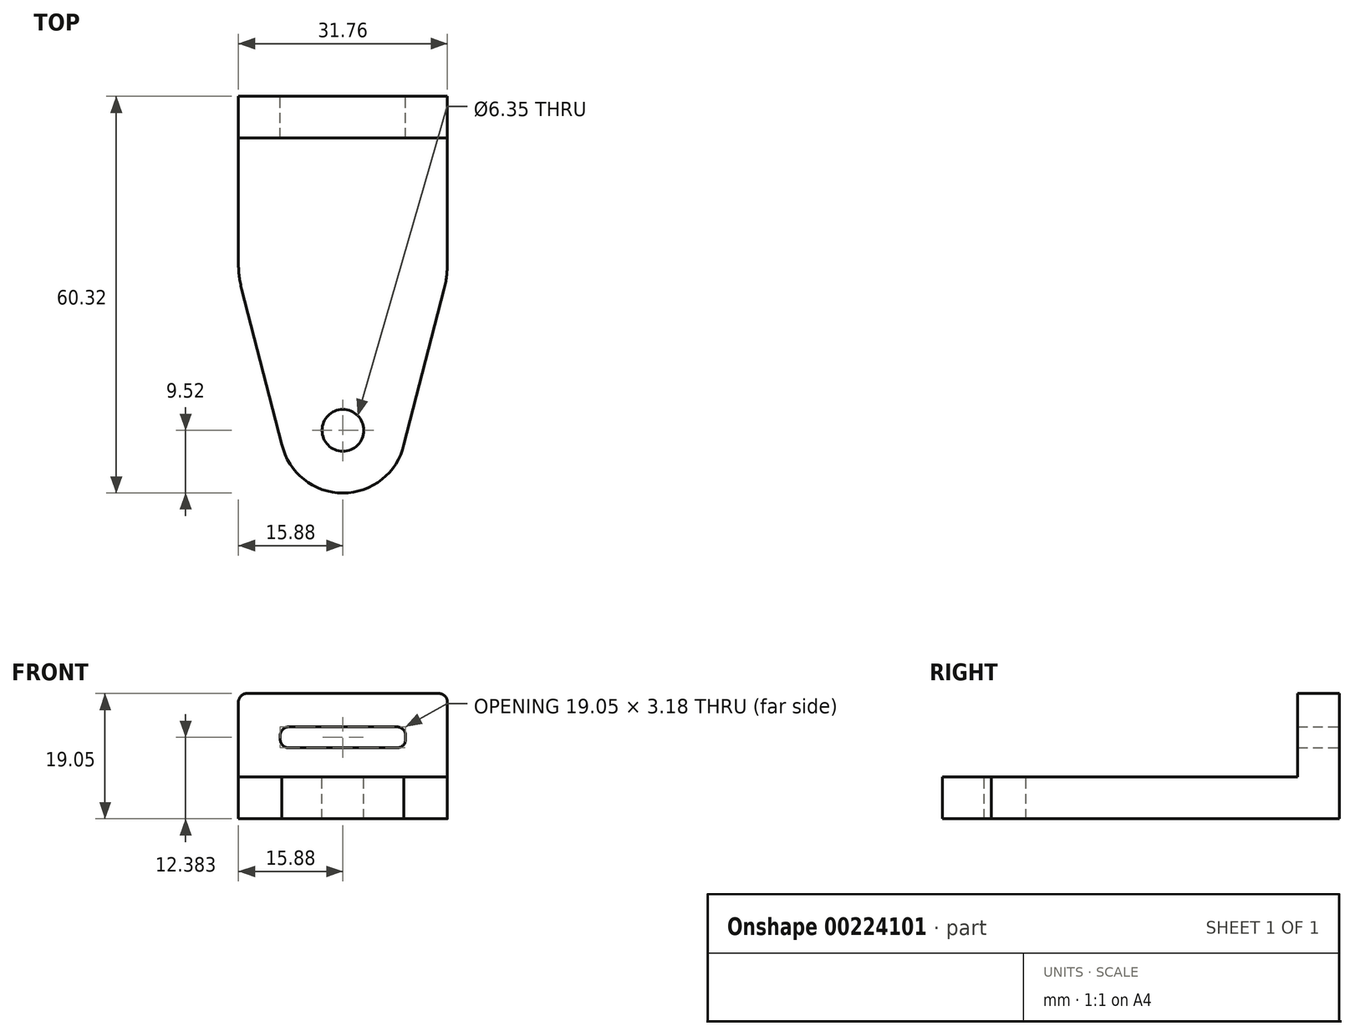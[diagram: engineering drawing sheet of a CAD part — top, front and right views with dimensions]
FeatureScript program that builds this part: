
annotation { "Feature Type Name" : "Feature", "Feature Type Description" : "" }
export const myFeature = defineFeature(function(context is Context, id is Id, definition is map)
    precondition{}
    {
        {
            var Q0;
            Q0=qCreatedBy(makeId("Top.planeOp"),FACE);
            var sketch = newSketch(context, id + "F0", { "sketchPlane" : qUnion([Q0])});
            skCircle(sketch, "E0", {"center": v(0, 0) * mm, "radius": 12.7 * mm});
            skCircle(sketch, "E1.0", {"center": v(0, 0) * mm, "radius": 15.88 * mm});
            skSolve(sketch);
        }
        {
            var Q0;
            Q0=makeQuery(id+"F0.imprint","IMPRINT",FACE,{"disambiguationData":[TD([[makeQuery(id+"F0.imprint","IMPRINT",EDGE,{"derivedFrom":sQuery(id+"F0.wireOp",EDGE,"E0")}),-1.0]])]});
            extrude(context, id + "F1", {"entities" : qUnion([Q0]), "depth" : 6.35 * mm});
        }
        {
            var Q0;
            Q0=qCreatedBy(makeId("Top.planeOp"),FACE);
            var sketch = newSketch(context, id + "F2", { "sketchPlane" : qUnion([Q0])});
            skLineSegment(sketch, "E2.bottom", {"start": v(-15.88, 0) * mm, "end": v(15.88, 0) * mm});
            skLineSegment(sketch, "E2.top", {"start": v(-15.88, 25.4) * mm, "end": v(15.87, 25.4) * mm});
            skLineSegment(sketch, "E2.left", {"start": v(-15.88, 0) * mm, "end": v(-15.88, 25.4) * mm});
            skLineSegment(sketch, "E2.right", {"start": v(15.88, 0) * mm, "end": v(15.87, 25.4) * mm});
            skSolve(sketch);
        }
        {
            var Q0;
            Q0=makeQuery(id+"F2.imprint","IMPRINT",FACE,{"disambiguationData":[TD([[makeQuery(id+"F2.imprint","IMPRINT",EDGE,{"derivedFrom":sQuery(id+"F2.wireOp",EDGE,"E2.bottom")}),1.0]])]});
            extrude(context, id + "F3", {"entities" : qUnion([Q0]), "operationType" : NewBodyOperationType.ADD, "depth" : 6.35 * mm});
        }
        {
            var Q0;
            {var subQ0=sQuery(id+"F2.wireOp",EDGE,"E2.top");var subQ1=sQuery(id+"F2.wireOp",EDGE,"E2.left");var subQ2=sQuery(id+"F2.wireOp",EDGE,"E2.right");Q0=makeQuery(id+"F3.boolean.opBoolean","SPLIT",FACE,{"disambiguationData":[TD([makeQuery(id+"F1.opExtrude","SWEPT_FACE",FACE,{"disambiguationData":[OSD([sQuery(id+"F0.wireOp",EDGE,"E1.0")])]})])],"derivedFrom":makeQuery(id+"F3.opExtrude","CAP_FACE",FACE,{"disambiguationData":[OSD([sQuery(id+"F2.wireOp",EDGE,"E2.bottom"),subQ0,subQ1,subQ2])],"isStart":false})});}
            var sketch = newSketch(context, id + "F4", { "sketchPlane" : qUnion([Q0])});
            skLineSegment(sketch, "E3.bottom", {"start": v(-15.88, 25.4) * mm, "end": v(15.87, 25.4) * mm});
            skLineSegment(sketch, "E3.top", {"start": v(-15.88, 19.05) * mm, "end": v(15.87, 19.05) * mm});
            skLineSegment(sketch, "E3.left", {"start": v(-15.88, 25.4) * mm, "end": v(-15.88, 19.05) * mm});
            skLineSegment(sketch, "E3.right", {"start": v(15.87, 25.4) * mm, "end": v(15.87, 19.05) * mm});
            skSolve(sketch);
        }
        {
            var Q0;
            Q0 = qSketchRegion(id + "F4", true);
            extrude(context, id + "F5", {"entities" : qUnion([Q0]), "operationType" : NewBodyOperationType.ADD, "depth" : 12.7 * mm});
        }
        {
            var Q0;
            Q0=makeQuery(id+"F5.boolean.opBoolean","MERGE",FACE,{"derivedFrom":[makeQuery(id+"F3.opExtrude","SWEPT_FACE",FACE,{"disambiguationData":[OSD([sQuery(id+"F2.wireOp",EDGE,"E2.top")])]}),makeQuery(id+"F5.opExtrude","SWEPT_FACE",FACE,{"disambiguationData":[OSD([sQuery(id+"F4.wireOp",EDGE,"E3.bottom")])]})]});
            var sketch = newSketch(context, id + "F6", { "sketchPlane" : qUnion([Q0])});
            skLineSegment(sketch, "E4.bottom", {"start": v(-9.53, 13.97) * mm, "end": v(9.53, 13.97) * mm});
            skLineSegment(sketch, "E4.top", {"start": v(-9.53, 10.8) * mm, "end": v(9.53, 10.8) * mm});
            skLineSegment(sketch, "E4.left", {"start": v(-9.53, 13.97) * mm, "end": v(-9.53, 10.8) * mm});
            skLineSegment(sketch, "E4.right", {"start": v(9.53, 13.97) * mm, "end": v(9.53, 10.8) * mm});
            skSolve(sketch);
        }
        {
            var Q0;
            Q0 = qSketchRegion(id + "F6", true);
            var Q1;
            Q1=makeQuery(id+"F5.opExtrude","SWEPT_FACE",FACE,{"disambiguationData":[OSD([sQuery(id+"F4.wireOp",EDGE,"E3.top")])]});
            extrude(context, id + "F7", {"entities" : qUnion([Q0]), "operationType" : NewBodyOperationType.REMOVE, "endBound" : BoundingType.UP_TO_SURFACE, "oppositeDirection" : true, "endBoundEntityFace" : qUnion([Q1]), "depth" : 25.4 * mm});
        }
        {
            var Q0;
            Q0=makeQuery(id+"F7.boolean.opBoolean","COPY",EDGE,{"derivedFrom":makeQuery(id+"F7.opExtrude","SWEPT_EDGE",EDGE,{"disambiguationData":[OSD([sQuery(id+"F6.wireOp",EDGE,"E4.bottom"),sQuery(id+"F6.wireOp",EDGE,"E4.right")])]})});
            var Q1;
            Q1=makeQuery(id+"F7.boolean.opBoolean","COPY",EDGE,{"derivedFrom":makeQuery(id+"F7.opExtrude","SWEPT_EDGE",EDGE,{"disambiguationData":[OSD([sQuery(id+"F6.wireOp",EDGE,"E4.bottom"),sQuery(id+"F6.wireOp",EDGE,"E4.left")])]})});
            var Q2;
            Q2=makeQuery(id+"F7.boolean.opBoolean","COPY",EDGE,{"derivedFrom":makeQuery(id+"F7.opExtrude","SWEPT_EDGE",EDGE,{"disambiguationData":[OSD([sQuery(id+"F6.wireOp",EDGE,"E4.top"),sQuery(id+"F6.wireOp",EDGE,"E4.left")])]})});
            var Q3;
            Q3=makeQuery(id+"F7.boolean.opBoolean","COPY",EDGE,{"derivedFrom":makeQuery(id+"F7.opExtrude","SWEPT_EDGE",EDGE,{"disambiguationData":[OSD([sQuery(id+"F6.wireOp",EDGE,"E4.top"),sQuery(id+"F6.wireOp",EDGE,"E4.right")])]})});
            var Q4;
            Q4=makeQuery(id+"F5.opExtrude","CAP_EDGE",EDGE,{"disambiguationData":[OSD([sQuery(id+"F4.wireOp",EDGE,"E3.right")])],"isStart":false});
            var Q5;
            Q5=makeQuery(id+"F5.opExtrude","CAP_EDGE",EDGE,{"disambiguationData":[OSD([sQuery(id+"F4.wireOp",EDGE,"E3.left")])],"isStart":false});
            fillet(context, id + "F8", {"entities" : qUnion([Q0, Q1, Q2, Q3, Q4, Q5]), "radius" : 1.27 * mm, "tangentPropagation" : true, "allowEdgeOverflow" : false});
        }
        {
            var Q0;
            Q0=makeQuery(id+"F3.boolean.opBoolean","MERGE",FACE,{"derivedFrom":[makeQuery(id+"F1.opExtrude","CAP_FACE",FACE,{"disambiguationData":[OSD([sQuery(id+"F0.wireOp",EDGE,"E0"),sQuery(id+"F0.wireOp",EDGE,"E1.0")])],"isStart":true}),makeQuery(id+"F3.opExtrude","CAP_FACE",FACE,{"disambiguationData":[OSD([sQuery(id+"F2.wireOp",EDGE,"E2.bottom"),sQuery(id+"F2.wireOp",EDGE,"E2.top"),sQuery(id+"F2.wireOp",EDGE,"E2.left"),sQuery(id+"F2.wireOp",EDGE,"E2.right")])],"isStart":true})]});
            var sketch = newSketch(context, id + "F9", { "sketchPlane" : qUnion([Q0])});
            skCircle(sketch, "E5", {"center": v(0, 0) * mm, "radius": 12.7 * mm});
            skSolve(sketch);
        }
        {
            var Q0;
            Q0 = qSketchRegion(id + "F9", true);
            extrude(context, id + "F10", {"entities" : qUnion([Q0]), "operationType" : NewBodyOperationType.ADD, "oppositeDirection" : true, "depth" : 6.35 * mm});
        }
        {
            var Q0;
            Q0=makeQuery(id+"F10.boolean.opBoolean","MERGE",FACE,{"derivedFrom":[makeQuery(id+"F3.boolean.opBoolean","MERGE",FACE,{"derivedFrom":[makeQuery(id+"F1.opExtrude","CAP_FACE",FACE,{"disambiguationData":[OSD([sQuery(id+"F0.wireOp",EDGE,"E0"),sQuery(id+"F0.wireOp",EDGE,"E1.0")])],"isStart":true}),makeQuery(id+"F3.opExtrude","CAP_FACE",FACE,{"disambiguationData":[OSD([sQuery(id+"F2.wireOp",EDGE,"E2.bottom"),sQuery(id+"F2.wireOp",EDGE,"E2.top"),sQuery(id+"F2.wireOp",EDGE,"E2.left"),sQuery(id+"F2.wireOp",EDGE,"E2.right")])],"isStart":true})]}),makeQuery(id+"F10.opExtrude","CAP_FACE",FACE,{"disambiguationData":[OSD([sQuery(id+"F9.wireOp",EDGE,"E5")])],"isStart":true})]});
            var sketch = newSketch(context, id + "F11", { "sketchPlane" : qUnion([Q0])});
            skCircle(sketch, "E6", {"center": v(0, 25.4) * mm, "radius": 9.53 * mm});
            skLineSegment(sketch, "E7", {"start": v(9.28, 27.54) * mm, "end": v(15.37, 3.97) * mm});
            skLineSegment(sketch, "E8", {"start": v(-9.28, 27.54) * mm, "end": v(-15.37, 3.97) * mm});
            skSolve(sketch);
        }
        {
            var Q0;
            {var subQ0=sQuery(id+"F11.wireOp",EDGE,"E8");Q0=makeQuery(id+"F11.imprint","IMPRINT",FACE,{"disambiguationData":[TD([[makeQuery(id+"F11.imprint","IMPRINT",EDGE,{"derivedFrom":subQ0}),1.0]])]});}
            var Q1;
            {var subQ0=sQuery(id+"F11.wireOp",EDGE,"E6");var subQ1=makeQuery(id+"F11.imprint","INTERSECT",VERTEX,{"derivedFrom":[subQ0,sQuery(id+"F11.wireOp",EDGE,"E7")]});Q1=makeQuery(id+"F11.imprint","IMPRINT",FACE,{"disambiguationData":[TD([[makeQuery(id+"F11.imprint","IMPRINT",EDGE,{"disambiguationData":[TD([[subQ1,-1.0]])],"derivedFrom":subQ0}),1.0]])]});}
            var Q2;
            {var subQ0=sQuery(id+"F11.wireOp",EDGE,"E7");Q2=makeQuery(id+"F11.imprint","IMPRINT",FACE,{"disambiguationData":[TD([[makeQuery(id+"F11.imprint","IMPRINT",EDGE,{"derivedFrom":subQ0}),-1.0]])]});}
            extrude(context, id + "F12", {"entities" : qUnion([Q0, Q1, Q2]), "operationType" : NewBodyOperationType.ADD, "oppositeDirection" : true, "depth" : 6.35 * mm});
        }
        {
            var Q0;
            Q0=makeQuery(id+"F12.opExtrude","CAP_FACE",FACE,{"disambiguationData":[OSD([sQuery(id+"F0.wireOp",EDGE,"E1.0"),sQuery(id+"F11.wireOp",EDGE,"E6"),sQuery(id+"F11.wireOp",EDGE,"E7"),sQuery(id+"F11.wireOp",EDGE,"E8")])],"isStart":false});
            var sketch = newSketch(context, id + "F13", { "sketchPlane" : qUnion([Q0])});
            skArc(sketch, "E9.0", {"start": v(9.28, -27.54) * mm, "mid": v(0, -34.92) * mm, "end": v(-9.28, -27.54) * mm, "construction": true});
            skCircle(sketch, "E10", {"center": v(0, -25.4) * mm, "radius": 3.18 * mm});
            skSolve(sketch);
        }
        {
            var Q0;
            Q0=makeQuery(id+"F13.imprint","IMPRINT",FACE,{"disambiguationData":[TD([[makeQuery(id+"F13.imprint","IMPRINT",EDGE,{"derivedFrom":sQuery(id+"F13.wireOp",EDGE,"E10")}),1.0]])]});
            var Q1;
            {var subQ0=sQuery(id+"F0.wireOp",EDGE,"E1.0");Q1=makeQuery(id+"F12.boolean.opBoolean","MERGE",FACE,{"derivedFrom":[makeQuery(id+"F10.boolean.opBoolean","MERGE",FACE,{"derivedFrom":[makeQuery(id+"F3.boolean.opBoolean","MERGE",FACE,{"derivedFrom":[makeQuery(id+"F1.opExtrude","CAP_FACE",FACE,{"disambiguationData":[OSD([sQuery(id+"F0.wireOp",EDGE,"E0"),subQ0])],"isStart":true}),makeQuery(id+"F3.opExtrude","CAP_FACE",FACE,{"disambiguationData":[OSD([sQuery(id+"F2.wireOp",EDGE,"E2.bottom"),sQuery(id+"F2.wireOp",EDGE,"E2.top"),sQuery(id+"F2.wireOp",EDGE,"E2.left"),sQuery(id+"F2.wireOp",EDGE,"E2.right")])],"isStart":true})]}),makeQuery(id+"F10.opExtrude","CAP_FACE",FACE,{"disambiguationData":[OSD([sQuery(id+"F9.wireOp",EDGE,"E5")])],"isStart":true})]}),makeQuery(id+"F12.opExtrude","CAP_FACE",FACE,{"disambiguationData":[OSD([subQ0,sQuery(id+"F11.wireOp",EDGE,"E6"),sQuery(id+"F11.wireOp",EDGE,"E7"),sQuery(id+"F11.wireOp",EDGE,"E8")])],"isStart":true})]});}
            extrude(context, id + "F14", {"entities" : qUnion([Q0]), "operationType" : NewBodyOperationType.REMOVE, "endBound" : BoundingType.UP_TO_SURFACE, "oppositeDirection" : true, "endBoundEntityFace" : qUnion([Q1]), "depth" : 25.4 * mm});
        }
    });
